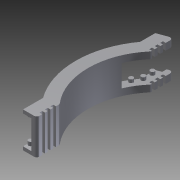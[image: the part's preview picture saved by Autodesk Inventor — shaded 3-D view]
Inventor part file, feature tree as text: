
AUTODESK INVENTOR PART (.ipt)
format: ipt  version: 2013 (Build 170138000, 138)  size: 257,536 bytes
history: native  units: in
note: dims shown in document units (in); Inventor stores cm internally (conversion verified against a paired STEP export)
features: reference x29, plane x6, sketch x6, extrude x6, pattern_linear x2, mirror x1, fillet x1
ambient origin geometry x8: Origin, YZ Plane, XZ Plane, XY Plane, X Axis, Y Axis, Z Axis, Center Point
bodies: Solid1 (feature_tree)
feature tree (51):
  plane  "Work Plane2"
  sketch  "Sketch3"  dims[d4=0.0625in d5=0.0in d6=0.125in d7=0.0in]
  plane  "Work Plane3"
  extrude  "Extrusion1"  Depth=0.125in TaperAngle=0.0deg
  sketch  "Sketch4"  dims[d8=0.25in d9=0.0in d10=0.0in]
  plane  "Work Plane4"
  extrude  "Extrusion2"  TaperAngle=0.0deg  [1 undecoded]
  plane  "Work Plane5"
  mirror  "Mirror1"
  extrude  "Extrusion3"  Depth=0.05in
  sketch  "Sketch7"  dims[d15=0.1in d16=0.05in d17=0.3125in d18=0.0in]
  plane  "Work Plane6"
  plane  "Work Plane7"
  extrude  "Extrusion7"  Depth=0.05in
  fillet  "Fillet1"  Radius=0.3125in
  extrude  "Extrusion5"  Depth=0.05in
  pattern_linear  "Rectangular Pattern1"  Count1=3 Spacing1=0.1in
  extrude  "Extrusion6"  Depth=0.05in
  pattern_linear  "Rectangular Pattern2"  Spacing1=0.4375in  [1 undecoded]
  reference  "Reference10"
  reference  "Reference11"
  reference  "Reference12"
  reference  "Reference13"
  reference  "Reference14"
  reference  "Reference15"
  reference  "Reference16"
  reference  "Reference17"
  reference  "Reference18"
  reference  "Reference19"
  reference  "Reference20"
  reference  "Reference21"
  reference  "Reference22"
  reference  "Reference23"
  reference  "Reference24"
  reference  "Reference25"
  reference  "Reference26"
  reference  "Reference27"
  reference  "Reference28"
  reference  "Reference29"
  reference  "Reference30"
  reference  "Reference31"
  reference  "Reference32"
  reference  "Reference33"
  sketch  "Sketch6"  dims[d13=0.05in d14=0.05in]
  reference  "Reference34"
  reference  "Reference35"
  reference  "Reference36"
  reference  "Reference37"
  reference  "Reference38"
  sketch  "Sketch8"  dims[d19=1.1811in d21=0.1in d22=0.05in]
  sketch  "Sketch9"  dims[d23=0.75in d24=0.0in d25=1.1811in d27=0.1in d28=0.05in d29=0.4375in d30=0.0in]
note: 2 required parameter values undecoded (feature->parameter linkage not recoverable at this tier; creation-order binding heuristic only, values carry confidence <= 0.55)
